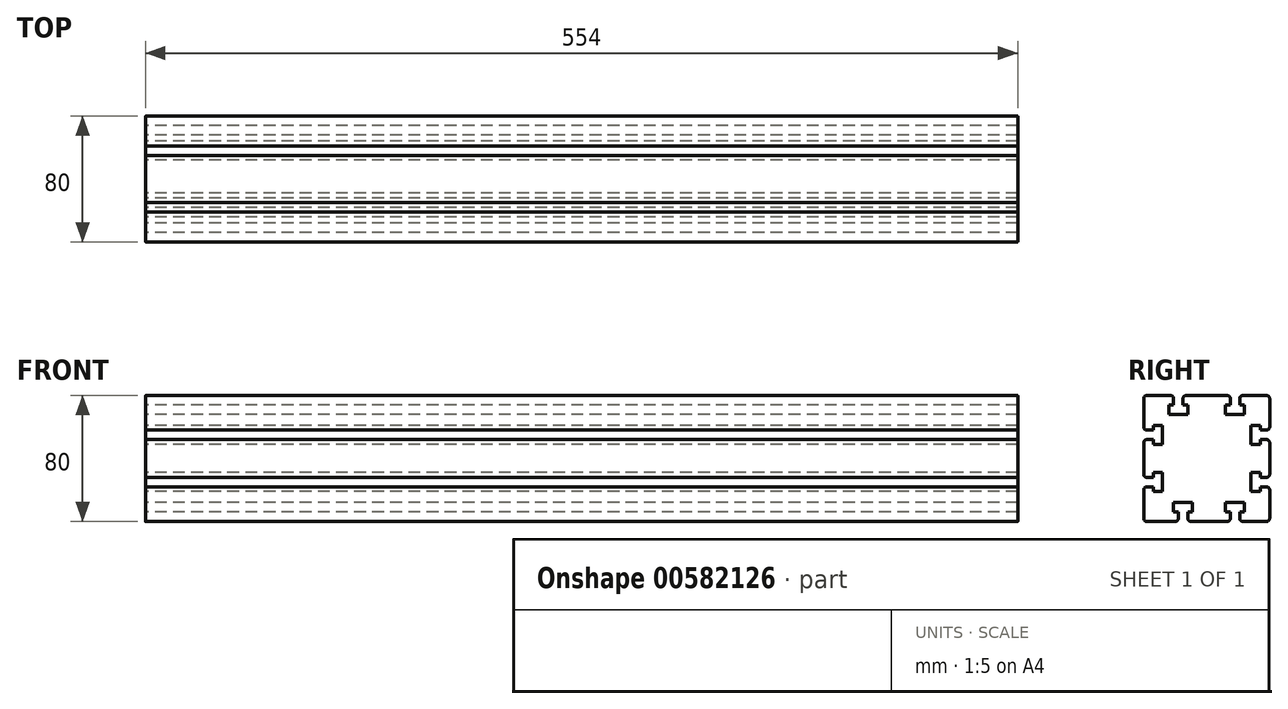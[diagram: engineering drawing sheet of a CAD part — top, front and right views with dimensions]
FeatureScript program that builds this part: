
annotation { "Feature Type Name" : "Feature", "Feature Type Description" : "" }
export const myFeature = defineFeature(function(context is Context, id is Id, definition is map)
    precondition{}
    {
        {
            var Q0;
            Q0=qCreatedBy(makeId("Right.planeOp"),FACE);
            var sketch = newSketch(context, id + "F0", { "sketchPlane" : qUnion([Q0])});
            skLineSegment(sketch, "E0.bottom", {"start": v(-40, 40) * mm, "end": v(-21, 40) * mm});
            skLineSegment(sketch, "E0.top", {"start": v(-40, -40) * mm, "end": v(-18, -40) * mm});
            skLineSegment(sketch, "E0.left", {"start": v(-40, 40) * mm, "end": v(-40, 18) * mm});
            skLineSegment(sketch, "E0.right", {"start": v(40, 40) * mm, "end": v(40, 18) * mm});
            skPoint(sketch, "E0.middle", {"position": v(0, 0) * mm});
            skLineSegment(sketch, "E1.left", {"start": v(15, 34) * mm, "end": v(15, 40) * mm});
            skLineSegment(sketch, "E1.right", {"start": v(21, 34) * mm, "end": v(21, 40) * mm});
            skPoint(sketch, "E1.middle", {"position": v(18, 40) * mm});
            skLineSegment(sketch, "E2.bottom", {"start": v(24, 34) * mm, "end": v(21, 34) * mm});
            skLineSegment(sketch, "E2.top", {"start": v(24, 28) * mm, "end": v(12, 28) * mm});
            skLineSegment(sketch, "E2.left", {"start": v(24, 34) * mm, "end": v(24, 28) * mm});
            skLineSegment(sketch, "E2.right", {"start": v(12, 34) * mm, "end": v(12, 28) * mm});
            skPoint(sketch, "E2.middle", {"position": v(18, 31) * mm});
            skPoint(sketch, "E2.middle.positionSnap0", {"position": v(18, 34) * mm});
            skPoint(sketch, "E2.centerSnap0", {"position": v(18, 34) * mm});
            skLineSegment(sketch, "E3.left", {"start": v(-21, 34) * mm, "end": v(-21, 40) * mm});
            skLineSegment(sketch, "E3.right", {"start": v(-15, 34) * mm, "end": v(-15, 40) * mm});
            skPoint(sketch, "E3.middle", {"position": v(-18, 40) * mm});
            skLineSegment(sketch, "E4.bottom", {"start": v(-24, 34) * mm, "end": v(-21, 34) * mm});
            skLineSegment(sketch, "E4.top", {"start": v(-24, 28) * mm, "end": v(-12, 28) * mm});
            skLineSegment(sketch, "E4.left", {"start": v(-24, 34) * mm, "end": v(-24, 28) * mm});
            skLineSegment(sketch, "E4.right", {"start": v(-12, 34) * mm, "end": v(-12, 28) * mm});
            skPoint(sketch, "E4.middle", {"position": v(-18, 31) * mm});
            skLineSegment(sketch, "E5.left", {"start": v(15, -34) * mm, "end": v(15, -40) * mm});
            skLineSegment(sketch, "E5.right", {"start": v(21, -34) * mm, "end": v(21, -40) * mm});
            skPoint(sketch, "E5.middle", {"position": v(18, -40) * mm});
            skLineSegment(sketch, "E6.bottom", {"start": v(12, -34) * mm, "end": v(15, -34) * mm});
            skLineSegment(sketch, "E6.top", {"start": v(12, -28) * mm, "end": v(24, -28) * mm});
            skLineSegment(sketch, "E6.left", {"start": v(12, -34) * mm, "end": v(12, -28) * mm});
            skLineSegment(sketch, "E6.right", {"start": v(24, -34) * mm, "end": v(24, -28) * mm});
            skPoint(sketch, "E6.middle", {"position": v(18, -31) * mm});
            skPoint(sketch, "E6.middle.positionSnap0", {"position": v(18, -34) * mm});
            skPoint(sketch, "E6.centerSnap0", {"position": v(18, -34) * mm});
            skLineSegment(sketch, "E7.left", {"start": v(-18, -40) * mm, "end": v(-18, -34) * mm});
            skLineSegment(sketch, "E7.right", {"start": v(-12, -40) * mm, "end": v(-12, -34) * mm});
            skPoint(sketch, "E7.middle", {"position": v(-15, -40) * mm});
            skLineSegment(sketch, "E8.bottom", {"start": v(-21, -34) * mm, "end": v(-18, -34) * mm});
            skLineSegment(sketch, "E8.top", {"start": v(-21, -28) * mm, "end": v(-9, -28) * mm});
            skLineSegment(sketch, "E8.left", {"start": v(-21, -34) * mm, "end": v(-21, -28) * mm});
            skLineSegment(sketch, "E8.right", {"start": v(-9, -34) * mm, "end": v(-9, -28) * mm});
            skPoint(sketch, "E8.middle", {"position": v(-15, -31) * mm});
            skPoint(sketch, "E8.middle.positionSnap0", {"position": v(-15, -34) * mm});
            skPoint(sketch, "E8.centerSnap0", {"position": v(-15, -34) * mm});
            skLineSegment(sketch, "E9.bottom", {"start": v(34, -18) * mm, "end": v(40, -18) * mm});
            skLineSegment(sketch, "E9.top", {"start": v(34, -12) * mm, "end": v(40, -12) * mm});
            skPoint(sketch, "E9.middle", {"position": v(40, -15) * mm});
            skLineSegment(sketch, "E10.bottom", {"start": v(34, -9) * mm, "end": v(28, -9) * mm});
            skLineSegment(sketch, "E10.top", {"start": v(34, -21) * mm, "end": v(28, -21) * mm});
            skLineSegment(sketch, "E10.left", {"start": v(34, -9) * mm, "end": v(34, -12) * mm});
            skLineSegment(sketch, "E10.right", {"start": v(28, -9) * mm, "end": v(28, -21) * mm});
            skPoint(sketch, "E10.middle", {"position": v(31, -15) * mm});
            skPoint(sketch, "E10.middle.positionSnap0", {"position": v(34, -15) * mm});
            skPoint(sketch, "E10.centerSnap0", {"position": v(34, -15) * mm});
            skLineSegment(sketch, "E11.bottom", {"start": v(34, 12) * mm, "end": v(40, 12) * mm});
            skLineSegment(sketch, "E11.top", {"start": v(34, 18) * mm, "end": v(40, 18) * mm});
            skPoint(sketch, "E11.middle", {"position": v(40, 15) * mm});
            skLineSegment(sketch, "E12.bottom", {"start": v(34, 21) * mm, "end": v(28, 21) * mm});
            skLineSegment(sketch, "E12.top", {"start": v(34, 9) * mm, "end": v(28, 9) * mm});
            skLineSegment(sketch, "E12.left", {"start": v(34, 21) * mm, "end": v(34, 18) * mm});
            skLineSegment(sketch, "E12.right", {"start": v(28, 21) * mm, "end": v(28, 9) * mm});
            skPoint(sketch, "E12.middle", {"position": v(31, 15) * mm});
            skPoint(sketch, "E12.middle.positionSnap0", {"position": v(34, 15) * mm});
            skPoint(sketch, "E12.cornerSnap0", {"position": v(34, 15) * mm});
            skPoint(sketch, "E12.centerSnap0", {"position": v(34, 15) * mm});
            skLineSegment(sketch, "E13.bottom", {"start": v(-40, 12) * mm, "end": v(-34, 12) * mm});
            skLineSegment(sketch, "E13.top", {"start": v(-40, 18) * mm, "end": v(-34, 18) * mm});
            skPoint(sketch, "E13.middle", {"position": v(-40, 15) * mm});
            skLineSegment(sketch, "E14.bottom", {"start": v(-34, 9) * mm, "end": v(-28, 9) * mm});
            skLineSegment(sketch, "E14.top", {"start": v(-34, 21) * mm, "end": v(-28, 21) * mm});
            skLineSegment(sketch, "E14.left", {"start": v(-34, 9) * mm, "end": v(-34, 12) * mm});
            skLineSegment(sketch, "E14.right", {"start": v(-28, 9) * mm, "end": v(-28, 21) * mm});
            skPoint(sketch, "E14.middle", {"position": v(-31, 15) * mm});
            skPoint(sketch, "E14.middle.positionSnap0", {"position": v(-34, 15) * mm});
            skPoint(sketch, "E14.centerSnap0", {"position": v(-34, 15) * mm});
            skLineSegment(sketch, "E15.bottom", {"start": v(-40, -18) * mm, "end": v(-34, -18) * mm});
            skLineSegment(sketch, "E15.top", {"start": v(-40, -12) * mm, "end": v(-34, -12) * mm});
            skPoint(sketch, "E15.middle", {"position": v(-40, -15) * mm});
            skLineSegment(sketch, "E16.bottom", {"start": v(-34, -9) * mm, "end": v(-28, -9) * mm});
            skLineSegment(sketch, "E16.top", {"start": v(-34, -21) * mm, "end": v(-28, -21) * mm});
            skLineSegment(sketch, "E16.left", {"start": v(-34, -9) * mm, "end": v(-34, -12) * mm});
            skLineSegment(sketch, "E16.right", {"start": v(-28, -9) * mm, "end": v(-28, -21) * mm});
            skPoint(sketch, "E16.middle", {"position": v(-31, -15) * mm});
            skPoint(sketch, "E16.middle.positionSnap0", {"position": v(-34, -15) * mm});
            skPoint(sketch, "E16.centerSnap0", {"position": v(-34, -15) * mm});
            skPoint(sketch, "E1.top.end.orphan", {"position": v(21, 46) * mm});
            skPoint(sketch, "E17.orphan", {"position": v(15, 46) * mm});
            skLineSegment(sketch, "E18.trimOffspring", {"start": v(21, 40) * mm, "end": v(40, 40) * mm});
            skLineSegment(sketch, "E19.trimOffspring", {"start": v(15, 34) * mm, "end": v(12, 34) * mm});
            skLineSegment(sketch, "E20.trimOffspring", {"start": v(-15, 34) * mm, "end": v(-12, 34) * mm});
            skLineSegment(sketch, "E21", {"start": v(15, 40) * mm, "end": v(-15, 40) * mm});
            skPoint(sketch, "E22.orphan", {"position": v(-15, 46) * mm});
            skPoint(sketch, "E23.orphan", {"position": v(-21, 46) * mm});
            skLineSegment(sketch, "E24.trimOffspring", {"start": v(-34, 18) * mm, "end": v(-34, 21) * mm});
            skLineSegment(sketch, "E25.trimOffspring", {"start": v(-40, 12) * mm, "end": v(-40, -12) * mm});
            skPoint(sketch, "E26.orphan", {"position": v(-46, 18) * mm});
            skPoint(sketch, "E27.orphan", {"position": v(-46, 12) * mm});
            skLineSegment(sketch, "E28.trimOffspring", {"start": v(-34, -18) * mm, "end": v(-34, -21) * mm});
            skLineSegment(sketch, "E29.trimOffspring", {"start": v(-40, -18) * mm, "end": v(-40, -40) * mm});
            skPoint(sketch, "E15.left.end.orphan", {"position": v(-46, -12) * mm});
            skPoint(sketch, "E15.left.start.orphan", {"position": v(-46, -18) * mm});
            skPoint(sketch, "E7.bottom.end.orphan", {"position": v(-12, -46) * mm});
            skPoint(sketch, "E30.orphan", {"position": v(-18, -46) * mm});
            skLineSegment(sketch, "E31.trimOffspring", {"start": v(-12, -40) * mm, "end": v(15, -40) * mm});
            skLineSegment(sketch, "E32.trimOffspring", {"start": v(-12, -34) * mm, "end": v(-9, -34) * mm});
            skLineSegment(sketch, "E33.trimOffspring", {"start": v(21, -40) * mm, "end": v(40, -40) * mm});
            skLineSegment(sketch, "E34.trimOffspring", {"start": v(21, -34) * mm, "end": v(24, -34) * mm});
            skPoint(sketch, "E35.orphan", {"position": v(21, -46) * mm});
            skPoint(sketch, "E36.orphan", {"position": v(15, -46) * mm});
            skPoint(sketch, "E9.right.end.orphan", {"position": v(46, -12) * mm});
            skPoint(sketch, "E9.right.start.orphan", {"position": v(46, -18) * mm});
            skLineSegment(sketch, "E37.trimOffspring", {"start": v(40, -18) * mm, "end": v(40, -40) * mm});
            skLineSegment(sketch, "E38.trimOffspring", {"start": v(34, -18) * mm, "end": v(34, -21) * mm});
            skLineSegment(sketch, "E39.trimOffspring", {"start": v(34, 12) * mm, "end": v(34, 9) * mm});
            skLineSegment(sketch, "E40.trimOffspring", {"start": v(40, 12) * mm, "end": v(40, -12) * mm});
            skPoint(sketch, "E41.orphan", {"position": v(46, 12) * mm});
            skPoint(sketch, "E42.orphan", {"position": v(46, 18) * mm});
            skSolve(sketch);
        }
        {
            var Q0;
            Q0=qSketchRegion(id+"F0",true);
            extrude(context, id + "F1", {"entities" : qUnion([Q0]), "depth" : 554 * mm, "offsetDistance" : 25 * mm});
        }
        {
            var Q0;
            Q0=makeQuery(id+"F1.opExtrude","SWEPT_EDGE",EDGE,{"disambiguationData":[OSD([sQuery(id+"F0.wireOp",EDGE,"E0.right"),sQuery(id+"F0.wireOp",EDGE,"E18.trimOffspring")])]});
            var Q1;
            Q1=makeQuery(id+"F1.opExtrude","SWEPT_EDGE",EDGE,{"disambiguationData":[OSD([sQuery(id+"F0.wireOp",EDGE,"E33.trimOffspring"),sQuery(id+"F0.wireOp",EDGE,"E37.trimOffspring")])]});
            var Q2;
            Q2=makeQuery(id+"F1.opExtrude","SWEPT_EDGE",EDGE,{"disambiguationData":[OSD([sQuery(id+"F0.wireOp",EDGE,"E0.bottom"),sQuery(id+"F0.wireOp",EDGE,"E0.left")])]});
            var Q3;
            Q3=makeQuery(id+"F1.opExtrude","SWEPT_EDGE",EDGE,{"disambiguationData":[OSD([sQuery(id+"F0.wireOp",EDGE,"E0.top"),sQuery(id+"F0.wireOp",EDGE,"E29.trimOffspring")])]});
            var Q4;
            Q4=makeQuery(id+"F1.opExtrude","SWEPT_EDGE",EDGE,{"disambiguationData":[OSD([sQuery(id+"F0.wireOp",EDGE,"E15.bottom"),sQuery(id+"F0.wireOp",EDGE,"E29.trimOffspring")])]});
            var Q5;
            Q5=makeQuery(id+"F1.opExtrude","SWEPT_EDGE",EDGE,{"disambiguationData":[OSD([sQuery(id+"F0.wireOp",EDGE,"E15.top"),sQuery(id+"F0.wireOp",EDGE,"E25.trimOffspring")])]});
            var Q6;
            Q6=makeQuery(id+"F1.opExtrude","SWEPT_EDGE",EDGE,{"disambiguationData":[OSD([sQuery(id+"F0.wireOp",EDGE,"E13.bottom"),sQuery(id+"F0.wireOp",EDGE,"E25.trimOffspring")])]});
            var Q7;
            Q7=makeQuery(id+"F1.opExtrude","SWEPT_EDGE",EDGE,{"disambiguationData":[OSD([sQuery(id+"F0.wireOp",EDGE,"E0.left"),sQuery(id+"F0.wireOp",EDGE,"E13.top")])]});
            var Q8;
            Q8=makeQuery(id+"F1.opExtrude","SWEPT_EDGE",EDGE,{"disambiguationData":[OSD([sQuery(id+"F0.wireOp",EDGE,"E1.right"),sQuery(id+"F0.wireOp",EDGE,"E18.trimOffspring")])]});
            var Q9;
            Q9=makeQuery(id+"F1.opExtrude","SWEPT_EDGE",EDGE,{"disambiguationData":[OSD([sQuery(id+"F0.wireOp",EDGE,"E1.left"),sQuery(id+"F0.wireOp",EDGE,"E21")])]});
            var Q10;
            Q10=makeQuery(id+"F1.opExtrude","SWEPT_EDGE",EDGE,{"disambiguationData":[OSD([sQuery(id+"F0.wireOp",EDGE,"E3.right"),sQuery(id+"F0.wireOp",EDGE,"E21")])]});
            var Q11;
            Q11=makeQuery(id+"F1.opExtrude","SWEPT_EDGE",EDGE,{"disambiguationData":[OSD([sQuery(id+"F0.wireOp",EDGE,"E0.bottom"),sQuery(id+"F0.wireOp",EDGE,"E3.left")])]});
            var Q12;
            Q12=makeQuery(id+"F1.opExtrude","SWEPT_EDGE",EDGE,{"disambiguationData":[OSD([sQuery(id+"F0.wireOp",EDGE,"E0.right"),sQuery(id+"F0.wireOp",EDGE,"E11.top")])]});
            var Q13;
            Q13=makeQuery(id+"F1.opExtrude","SWEPT_EDGE",EDGE,{"disambiguationData":[OSD([sQuery(id+"F0.wireOp",EDGE,"E11.bottom"),sQuery(id+"F0.wireOp",EDGE,"E40.trimOffspring")])]});
            var Q14;
            Q14=makeQuery(id+"F1.opExtrude","SWEPT_EDGE",EDGE,{"disambiguationData":[OSD([sQuery(id+"F0.wireOp",EDGE,"E9.top"),sQuery(id+"F0.wireOp",EDGE,"E40.trimOffspring")])]});
            var Q15;
            Q15=makeQuery(id+"F1.opExtrude","SWEPT_EDGE",EDGE,{"disambiguationData":[OSD([sQuery(id+"F0.wireOp",EDGE,"E9.bottom"),sQuery(id+"F0.wireOp",EDGE,"E37.trimOffspring")])]});
            var Q16;
            Q16=makeQuery(id+"F1.opExtrude","SWEPT_EDGE",EDGE,{"disambiguationData":[OSD([sQuery(id+"F0.wireOp",EDGE,"E5.right"),sQuery(id+"F0.wireOp",EDGE,"E33.trimOffspring")])]});
            var Q17;
            Q17=makeQuery(id+"F1.opExtrude","SWEPT_EDGE",EDGE,{"disambiguationData":[OSD([sQuery(id+"F0.wireOp",EDGE,"E5.left"),sQuery(id+"F0.wireOp",EDGE,"E31.trimOffspring")])]});
            var Q18;
            Q18=makeQuery(id+"F1.opExtrude","SWEPT_EDGE",EDGE,{"disambiguationData":[OSD([sQuery(id+"F0.wireOp",EDGE,"E7.right"),sQuery(id+"F0.wireOp",EDGE,"E31.trimOffspring")])]});
            var Q19;
            Q19=makeQuery(id+"F1.opExtrude","SWEPT_EDGE",EDGE,{"disambiguationData":[OSD([sQuery(id+"F0.wireOp",EDGE,"E0.top"),sQuery(id+"F0.wireOp",EDGE,"E7.left")])]});
            fillet(context, id + "F2", {"entities" : qUnion([Q0, Q1, Q2, Q3, Q4, Q5, Q6, Q7, Q8, Q9, Q10, Q11, Q12, Q13, Q14, Q15, Q16, Q17, Q18, Q19]), "radius" : 2 * mm, "tangentPropagation" : true, "allowEdgeOverflow" : false});
        }
    });
